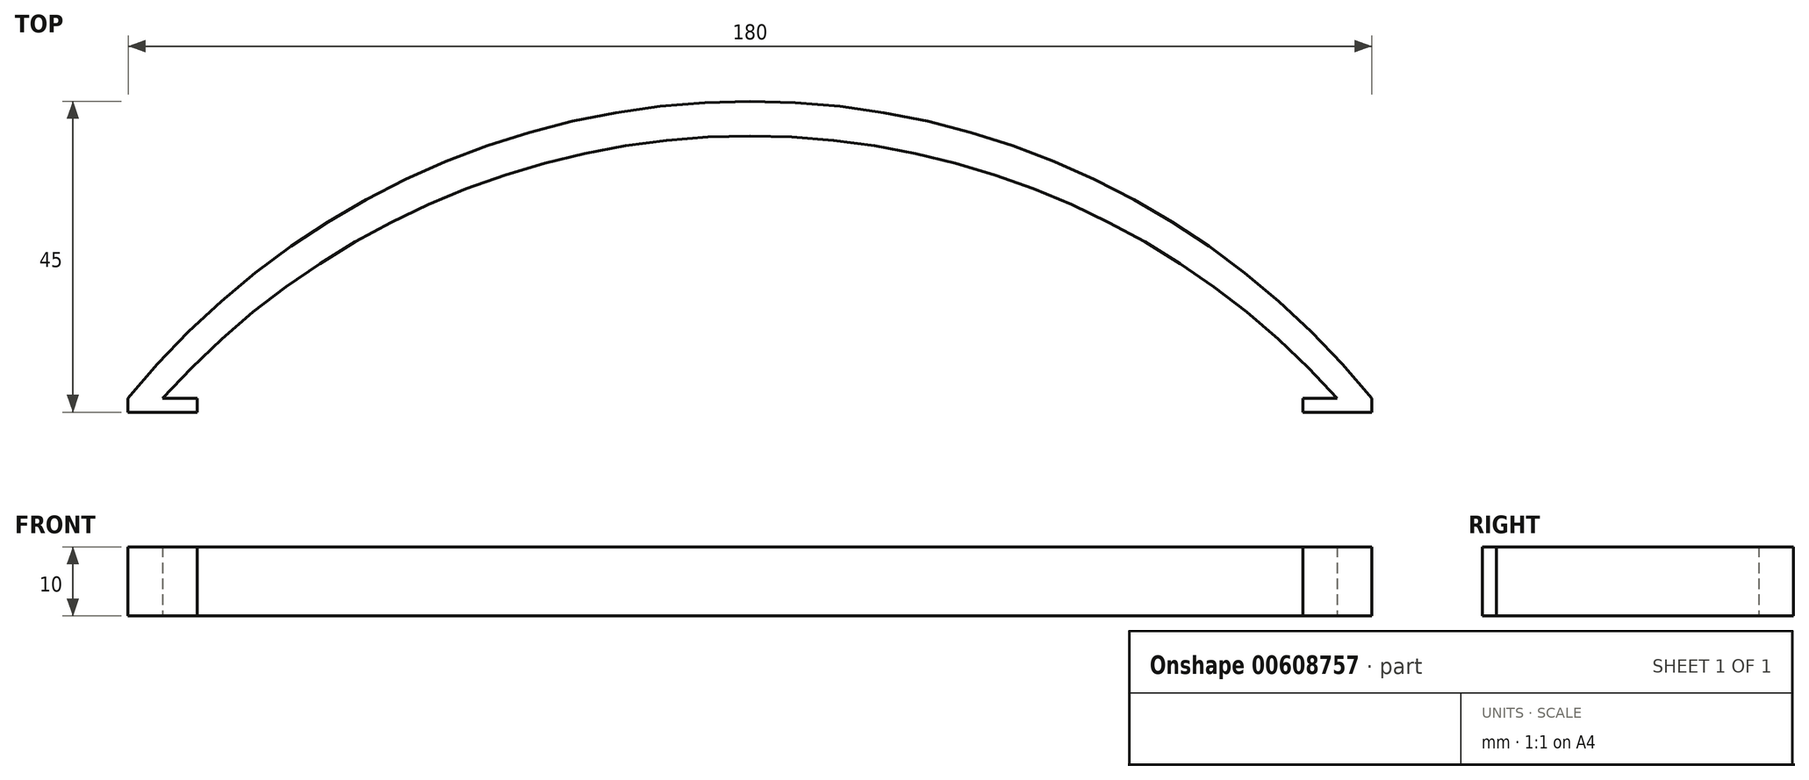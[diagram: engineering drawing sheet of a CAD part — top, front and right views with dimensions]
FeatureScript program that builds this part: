
annotation { "Feature Type Name" : "Feature", "Feature Type Description" : "" }
export const myFeature = defineFeature(function(context is Context, id is Id, definition is map)
    precondition{}
    {
        {
            var Q0;
            Q0=qCreatedBy(makeId("Top.planeOp"),FACE);
            var sketch = newSketch(context, id + "F0", { "sketchPlane" : qUnion([Q0])});
            skLineSegment(sketch, "E0.bottom", {"start": v(-98.43, 0) * mm, "end": v(-88.43, 0) * mm});
            skLineSegment(sketch, "E0.top", {"start": v(-98.43, -2) * mm, "end": v(-88.43, -2) * mm});
            skLineSegment(sketch, "E0.left", {"start": v(-98.43, 0) * mm, "end": v(-98.43, -2) * mm});
            skLineSegment(sketch, "E0.right", {"start": v(-88.43, 0) * mm, "end": v(-88.43, -2) * mm});
            skLineSegment(sketch, "E1", {"start": v(-88.43, -2) * mm, "end": v(71.57, -2) * mm, "construction": true});
            skLineSegment(sketch, "E2.bottom", {"start": v(71.57, -2) * mm, "end": v(81.57, -2) * mm});
            skLineSegment(sketch, "E2.top", {"start": v(71.57, 0) * mm, "end": v(81.57, 0) * mm});
            skLineSegment(sketch, "E2.left", {"start": v(71.57, -2) * mm, "end": v(71.57, 0) * mm});
            skLineSegment(sketch, "E2.right", {"start": v(81.57, -2) * mm, "end": v(81.57, 0) * mm});
            skLineSegment(sketch, "E3", {"start": v(-98.43, 0) * mm, "end": v(-93.43, 0) * mm, "construction": true});
            skLineSegment(sketch, "E4", {"start": v(81.57, 0) * mm, "end": v(76.57, 0) * mm, "construction": true});
            skArc(sketch, "E5", {"start": v(81.57, 0) * mm, "mid": v(-8.43, 43) * mm, "end": v(-98.43, 0) * mm});
            skArc(sketch, "E6", {"start": v(76.57, 0) * mm, "mid": v(-8.43, 38) * mm, "end": v(-93.43, 0) * mm});
            skSolve(sketch);
        }
        {
            var Q0;
            Q0 = qSketchRegion(id + "F0", true);
            extrude(context, id + "F1", {"entities" : qUnion([Q0]), "depth" : 10 * mm, "offsetDistance" : 25 * mm});
        }
    });
